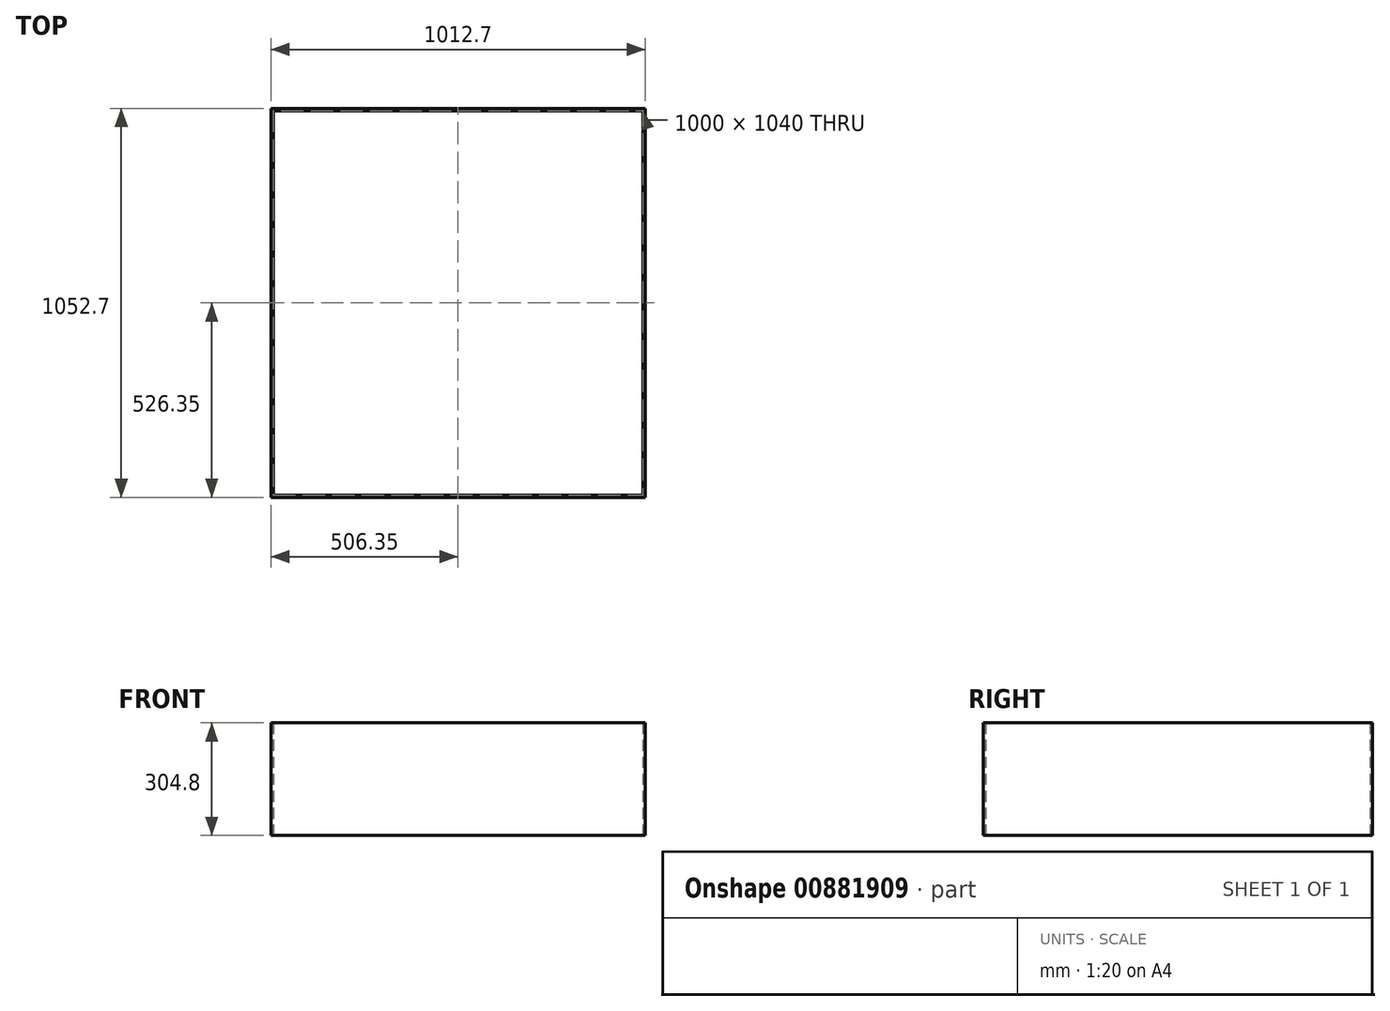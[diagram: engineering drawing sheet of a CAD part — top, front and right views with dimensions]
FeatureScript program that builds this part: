
annotation { "Feature Type Name" : "Feature", "Feature Type Description" : "" }
export const myFeature = defineFeature(function(context is Context, id is Id, definition is map)
    precondition{}
    {
        {
            var Q0;
            Q0=qCreatedBy(makeId("Top.planeOp"),FACE);
            var sketch = newSketch(context, id + "F0", { "sketchPlane" : qUnion([Q0])});
            skLineSegment(sketch, "E0.bottom", {"start": v(500, 520) * mm, "end": v(-500, 520) * mm});
            skLineSegment(sketch, "E0.top", {"start": v(500, -520) * mm, "end": v(-500, -520) * mm});
            skLineSegment(sketch, "E0.left", {"start": v(500, 520) * mm, "end": v(500, -520) * mm});
            skLineSegment(sketch, "E0.right", {"start": v(-500, 520) * mm, "end": v(-500, -520) * mm});
            skPoint(sketch, "E0.middle", {"position": v(0, 0) * mm});
            skLineSegment(sketch, "E1.bottom", {"start": v(-500, 520) * mm, "end": v(-506.35, 520) * mm});
            skLineSegment(sketch, "E1.top", {"start": v(-500, 526.35) * mm, "end": v(-506.35, 526.35) * mm});
            skLineSegment(sketch, "E1.left", {"start": v(-500, 520) * mm, "end": v(-500, 526.35) * mm});
            skLineSegment(sketch, "E1.right", {"start": v(-506.35, 520) * mm, "end": v(-506.35, 526.35) * mm});
            skLineSegment(sketch, "E2.bottom", {"start": v(500, 520) * mm, "end": v(506.35, 520) * mm});
            skLineSegment(sketch, "E2.top", {"start": v(500, 526.35) * mm, "end": v(506.35, 526.35) * mm});
            skLineSegment(sketch, "E2.left", {"start": v(500, 520) * mm, "end": v(500, 526.35) * mm});
            skLineSegment(sketch, "E2.right", {"start": v(506.35, 520) * mm, "end": v(506.35, 526.35) * mm});
            skLineSegment(sketch, "E3.bottom", {"start": v(500, -520) * mm, "end": v(506.35, -520) * mm});
            skLineSegment(sketch, "E3.top", {"start": v(500, -526.35) * mm, "end": v(506.35, -526.35) * mm});
            skLineSegment(sketch, "E3.left", {"start": v(500, -520) * mm, "end": v(500, -526.35) * mm});
            skLineSegment(sketch, "E3.right", {"start": v(506.35, -520) * mm, "end": v(506.35, -526.35) * mm});
            skLineSegment(sketch, "E4.bottom", {"start": v(-500, -520) * mm, "end": v(-506.35, -520) * mm});
            skLineSegment(sketch, "E4.top", {"start": v(-500, -526.35) * mm, "end": v(-506.35, -526.35) * mm});
            skLineSegment(sketch, "E4.left", {"start": v(-500, -520) * mm, "end": v(-500, -526.35) * mm});
            skLineSegment(sketch, "E4.right", {"start": v(-506.35, -520) * mm, "end": v(-506.35, -526.35) * mm});
            skLineSegment(sketch, "E5", {"start": v(-506.35, 520) * mm, "end": v(-506.35, -520) * mm});
            skLineSegment(sketch, "E6", {"start": v(-500, 526.35) * mm, "end": v(500, 526.35) * mm});
            skLineSegment(sketch, "E7", {"start": v(506.35, 520) * mm, "end": v(506.35, -520) * mm});
            skLineSegment(sketch, "E8", {"start": v(-500, -526.35) * mm, "end": v(500, -526.35) * mm});
            skSolve(sketch);
        }
        {
            var Q0;
            Q0=makeQuery(id+"F0.imprint","IMPRINT",FACE,{"disambiguationData":[TD([[makeQuery(id+"F0.imprint","IMPRINT",EDGE,{"derivedFrom":sQuery(id+"F0.wireOp",EDGE,"E1.bottom")}),-1.0]])]});
            var Q1;
            Q1=makeQuery(id+"F0.imprint","IMPRINT",FACE,{"disambiguationData":[TD([[makeQuery(id+"F0.imprint","IMPRINT",EDGE,{"derivedFrom":sQuery(id+"F0.wireOp",EDGE,"E2.bottom")}),1.0]])]});
            var Q2;
            Q2=makeQuery(id+"F0.imprint","IMPRINT",FACE,{"disambiguationData":[TD([[makeQuery(id+"F0.imprint","IMPRINT",EDGE,{"derivedFrom":sQuery(id+"F0.wireOp",EDGE,"E3.bottom")}),-1.0]])]});
            var Q3;
            Q3=makeQuery(id+"F0.imprint","IMPRINT",FACE,{"disambiguationData":[TD([[makeQuery(id+"F0.imprint","IMPRINT",EDGE,{"derivedFrom":sQuery(id+"F0.wireOp",EDGE,"E4.bottom")}),1.0]])]});
            var Q4;
            Q4=makeQuery(id+"F0.imprint","IMPRINT",FACE,{"disambiguationData":[TD([[makeQuery(id+"F0.imprint","IMPRINT",EDGE,{"derivedFrom":sQuery(id+"F0.wireOp",EDGE,"E0.bottom")}),-1.0]])]});
            var Q5;
            Q5=makeQuery(id+"F0.imprint","IMPRINT",FACE,{"disambiguationData":[TD([[makeQuery(id+"F0.imprint","IMPRINT",EDGE,{"derivedFrom":sQuery(id+"F0.wireOp",EDGE,"E0.top")}),1.0]])]});
            var Q6;
            Q6=makeQuery(id+"F0.imprint","IMPRINT",FACE,{"disambiguationData":[TD([[makeQuery(id+"F0.imprint","IMPRINT",EDGE,{"derivedFrom":sQuery(id+"F0.wireOp",EDGE,"E0.left")}),1.0]])]});
            var Q7;
            Q7=makeQuery(id+"F0.imprint","IMPRINT",FACE,{"disambiguationData":[TD([[makeQuery(id+"F0.imprint","IMPRINT",EDGE,{"derivedFrom":sQuery(id+"F0.wireOp",EDGE,"E0.right")}),-1.0]])]});
            extrude(context, id + "F1", {"entities" : qUnion([Q0, Q1, Q2, Q3, Q4, Q5, Q6, Q7]), "depth" : 304.8 * mm, "offsetDistance" : 25.4 * mm});
        }
    });
